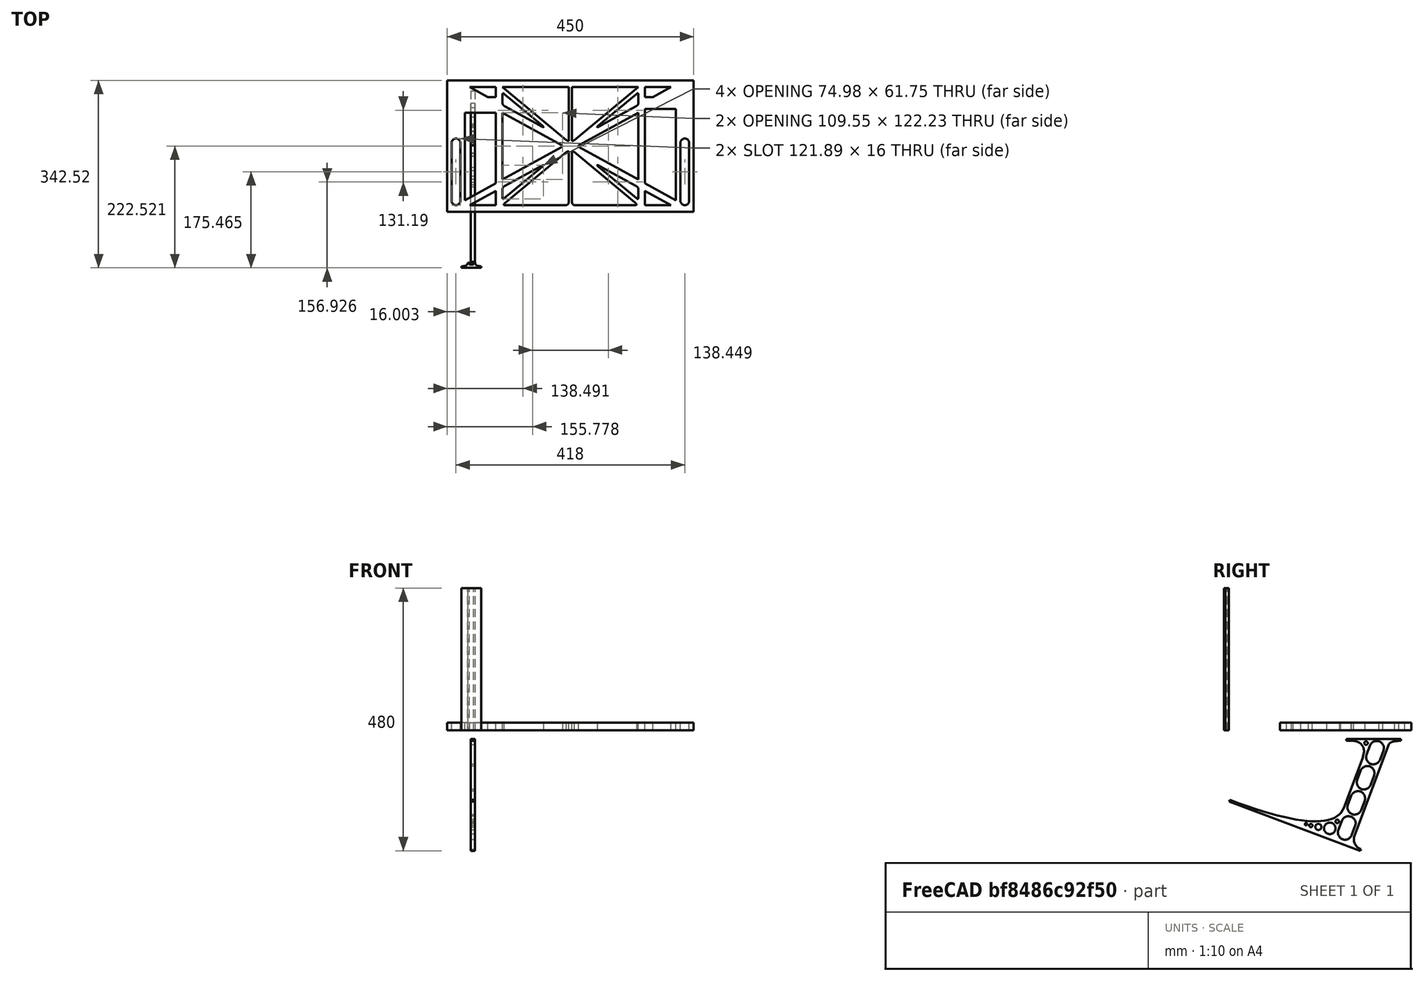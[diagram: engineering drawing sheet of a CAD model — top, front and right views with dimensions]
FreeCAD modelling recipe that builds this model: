
FCSTD DOCUMENT  (FreeCAD 0.19R0.19.2)
Label: laptopStand081
License: All rights reserved
LicenseURL: http://en.wikipedia.org/wiki/All_rights_reserved
objects: Sketcher::SketchObject×3, Part::Extrusion×3
note: 6 computed .brp shape members not serialized (recipe doc carries the construction recipe); baked Part::Feature solids carry a one-line shape summary decoded from their .brp

FEATURE [Sketcher::SketchObject] Sketch
  FullyConstrained = false
  sketch-geometry (204):
    g0: LineSegment StartX=-10.9272 StartY=-82.7794 StartZ=0 EndX=46.0728 EndY=-51.4823 EndZ=0
    g1: LineSegment StartX=366.073 StartY=-91.7794 StartZ=0 EndX=318.073 EndY=-65.424 EndZ=0
    g2: LineSegment StartX=-10.9272 StartY=77.3346 StartZ=0 EndX=-10.9272 EndY=-82.7794 EndZ=0
    g3: LineSegment StartX=375.073 StartY=-82.7794 StartZ=0 EndX=375.073 EndY=83.9235 EndZ=0
    g4: LineSegment StartX=-1.92719 StartY=-91.7794 StartZ=0 EndX=46.0728 EndY=-91.7794 EndZ=0
    g5: LineSegment StartX=318.073 StartY=124.221 StartZ=0 EndX=366.073 EndY=124.221 EndZ=0
    g6: LineSegment StartX=306.073 StartY=124.221 StartZ=0 EndX=189.124 EndY=27.0628 EndZ=0
    g7: LineSegment StartX=175.022 StartY=27.0628 StartZ=0 EndX=58.0728 EndY=124.221 EndZ=0
    g8: LineSegment StartX=306.073 StartY=77.3346 StartZ=0 EndX=306.073 EndY=-44.8935 EndZ=0
    g9: LineSegment StartX=318.073 StartY=83.9235 StartZ=0 EndX=318.073 EndY=-51.4823 EndZ=0
    g10: LineSegment StartX=318.073 StartY=-51.4823 StartZ=0 EndX=375.073 EndY=-82.7794 EndZ=0
    g11: LineSegment StartX=318.073 StartY=-65.424 StartZ=0 EndX=318.073 EndY=-91.7794 EndZ=0
    g12: LineSegment StartX=318.073 StartY=-91.7794 StartZ=0 EndX=366.073 EndY=-91.7794 EndZ=0
    g13: LineSegment StartX=58.0728 StartY=-44.8935 StartZ=0 EndX=58.0728 EndY=77.3346 EndZ=0
    g14: LineSegment StartX=46.0728 StartY=-65.424 StartZ=0 EndX=-1.92719 EndY=-91.7794 EndZ=0
    g15: LineSegment StartX=46.0728 StartY=-65.424 StartZ=0 EndX=46.0728 EndY=-91.7794 EndZ=0
    g16: LineSegment StartX=46.0728 StartY=77.3346 StartZ=0 EndX=46.0728 EndY=-51.4823 EndZ=0
    g17: LineSegment StartX=-42.9272 StartY=136.221 StartZ=0 EndX=-42.9272 EndY=-103.779 EndZ=0
    g18: LineSegment StartX=407.073 StartY=136.221 StartZ=0 EndX=407.073 EndY=-103.779 EndZ=0
    g19: LineSegment StartX=179.022 StartY=27.0628 StartZ=0 EndX=179.022 EndY=124.221 EndZ=0
    g20: LineSegment StartX=185.124 StartY=27.0628 StartZ=0 EndX=185.124 EndY=124.221 EndZ=0
    g21: ArcOfCircle CenterX=-26.9272 CenterY=22.1087 CenterZ=0 NormalX=0 NormalY=0 NormalZ=1 AngleXU=0 Radius=8 StartAngle=1e-16 EndAngle=3.14159
    g22: ArcOfCircle CenterX=-26.9272 CenterY=-83.7794 CenterZ=0 NormalX=0 NormalY=0 NormalZ=1 AngleXU=0 Radius=8 StartAngle=3.14159 EndAngle=6.28319
    g23: LineSegment StartX=-34.9272 StartY=22.1087 StartZ=0 EndX=-34.9272 EndY=-83.7794 EndZ=0
    g24: LineSegment StartX=-18.9272 StartY=22.1087 StartZ=0 EndX=-18.9272 EndY=-83.7794 EndZ=0
    g25: LineSegment StartX=306.073 StartY=124.221 StartZ=0 EndX=185.124 EndY=124.221 EndZ=0
    g26: LineSegment StartX=179.022 StartY=124.221 StartZ=0 EndX=58.0728 EndY=124.221 EndZ=0
    g27: ArcOfCircle CenterX=391.073 CenterY=22.1087 CenterZ=0 NormalX=0 NormalY=0 NormalZ=1 AngleXU=0 Radius=8 StartAngle=-4.4e-15 EndAngle=3.14159
    g28: LineSegment StartX=399.073 StartY=22.1087 StartZ=0 EndX=399.073 EndY=-83.7794 EndZ=0
    g29: LineSegment StartX=383.073 StartY=22.1087 StartZ=0 EndX=383.073 EndY=-83.7794 EndZ=0
    g30: ArcOfCircle CenterX=391.073 CenterY=-83.7794 CenterZ=0 NormalX=0 NormalY=0 NormalZ=1 AngleXU=0 Radius=8 StartAngle=3.14159 EndAngle=6.28319
    g31: Circle CenterX=175.022 CenterY=27.0628 CenterZ=0 NormalX=0 NormalY=0 NormalZ=1 AngleXU=0 Radius=1
    g32: Circle CenterX=179.022 CenterY=24.8665 CenterZ=0 NormalX=0 NormalY=0 NormalZ=1 AngleXU=0 Radius=1
    g33: Circle CenterX=179.022 CenterY=27.0628 CenterZ=0 NormalX=0 NormalY=0 NormalZ=1 AngleXU=0 Radius=1
    g34: BSplineCurve PolesCount=3 KnotsCount=2 Degree=2 IsPeriodic=0
    g35: GeomPoint X=175.022 Y=27.0628 Z=0
    g36: GeomPoint X=179.022 Y=27.0628 Z=0
    g37: Circle CenterX=189.124 CenterY=27.0628 CenterZ=0 NormalX=0 NormalY=0 NormalZ=1 AngleXU=0 Radius=1
    g38: Circle CenterX=185.124 CenterY=24.8665 CenterZ=0 NormalX=0 NormalY=0 NormalZ=1 AngleXU=0 Radius=1
    g39: Circle CenterX=185.124 CenterY=27.0628 CenterZ=0 NormalX=0 NormalY=0 NormalZ=1 AngleXU=0 Radius=1
    g40: BSplineCurve PolesCount=3 KnotsCount=2 Degree=2 IsPeriodic=0
    g41: GeomPoint X=189.124 Y=27.0628 Z=0
    g42: GeomPoint X=185.124 Y=27.0628 Z=0
    g43: Circle CenterX=175.022 CenterY=5.37834 CenterZ=0 NormalX=0 NormalY=0 NormalZ=1 AngleXU=0 Radius=1
    g44: Circle CenterX=179.022 CenterY=7.57463 CenterZ=0 NormalX=0 NormalY=0 NormalZ=1 AngleXU=0 Radius=1
    g45: Circle CenterX=179.022 CenterY=5.34704 CenterZ=0 NormalX=0 NormalY=0 NormalZ=1 AngleXU=0 Radius=1
    g46: BSplineCurve PolesCount=3 KnotsCount=2 Degree=2 IsPeriodic=0
    g47: GeomPoint X=175.022 Y=5.37834 Z=0
    g48: GeomPoint X=179.022 Y=5.34704 Z=0
    g49: Circle CenterX=189.124 CenterY=5.37834 CenterZ=0 NormalX=0 NormalY=0 NormalZ=1 AngleXU=0 Radius=1
    g50: Circle CenterX=185.124 CenterY=7.57463 CenterZ=0 NormalX=0 NormalY=0 NormalZ=1 AngleXU=0 Radius=1
    g51: Circle CenterX=185.124 CenterY=5.34704 CenterZ=0 NormalX=0 NormalY=0 NormalZ=1 AngleXU=0 Radius=1
    g52: BSplineCurve PolesCount=3 KnotsCount=2 Degree=2 IsPeriodic=0
    g53: GeomPoint X=189.124 Y=5.37834 Z=0
    g54: GeomPoint X=185.124 Y=5.34704 Z=0
    g55: Circle CenterX=165.871 CenterY=18.1458 CenterZ=0 NormalX=0 NormalY=0 NormalZ=1 AngleXU=0 Radius=1
    g56: Circle CenterX=169.377 CenterY=16.2206 CenterZ=0 NormalX=0 NormalY=0 NormalZ=1 AngleXU=0 Radius=1
    g57: Circle CenterX=165.871 CenterY=14.2954 CenterZ=0 NormalX=0 NormalY=0 NormalZ=1 AngleXU=0 Radius=1
    g58: BSplineCurve PolesCount=3 KnotsCount=2 Degree=2 IsPeriodic=0
    g59: GeomPoint X=165.871 Y=18.1458 Z=0
    g60: GeomPoint X=165.871 Y=14.2954 Z=0
    g61: Circle CenterX=198.275 CenterY=18.1458 CenterZ=0 NormalX=0 NormalY=0 NormalZ=1 AngleXU=0 Radius=1
    g62: Circle CenterX=194.768 CenterY=16.2206 CenterZ=0 NormalX=0 NormalY=0 NormalZ=1 AngleXU=0 Radius=1
    g63: Circle CenterX=198.275 CenterY=14.2954 CenterZ=0 NormalX=0 NormalY=0 NormalZ=1 AngleXU=0 Radius=1
    g64: BSplineCurve PolesCount=3 KnotsCount=2 Degree=2 IsPeriodic=0
    g65: GeomPoint X=198.275 Y=18.1458 Z=0
    g66: GeomPoint X=198.275 Y=14.2954 Z=0
    g67: LineSegment StartX=165.871 StartY=18.1458 StartZ=0 EndX=58.0728 EndY=77.3346 EndZ=0
    g68: LineSegment StartX=58.0728 StartY=-44.8935 StartZ=0 EndX=165.871 EndY=14.2954 EndZ=0
    g69: LineSegment StartX=198.275 StartY=18.1458 StartZ=0 EndX=306.073 EndY=77.3346 EndZ=0
    g70: LineSegment StartX=198.275 StartY=14.2954 StartZ=0 EndX=306.073 EndY=-44.8935 EndZ=0
    g71: LineSegment StartX=407.073 StartY=-103.779 StartZ=0 EndX=-42.9272 EndY=-103.779 EndZ=0
    g72: LineSegment StartX=407.073 StartY=136.221 StartZ=0 EndX=-42.9272 EndY=136.221 EndZ=0
    g73: LineSegment StartX=46.0728 StartY=77.3346 StartZ=0 EndX=-10.9272 EndY=77.3346 EndZ=0
    g74: LineSegment StartX=46.0728 StartY=105.865 StartZ=0 EndX=31.5028 EndY=105.865 EndZ=0
    g75: LineSegment StartX=46.0728 StartY=124.221 StartZ=0 EndX=46.0728 EndY=105.865 EndZ=0
    g76: LineSegment StartX=-1.92719 StartY=124.221 StartZ=0 EndX=31.5028 EndY=105.865 EndZ=0
    g77: LineSegment StartX=46.0728 StartY=124.221 StartZ=0 EndX=-1.92719 EndY=124.221 EndZ=0
    g78: LineSegment StartX=318.073 StartY=83.9235 StartZ=0 EndX=375.073 EndY=83.9235 EndZ=0
    g79: LineSegment StartX=318.073 StartY=105.865 StartZ=0 EndX=332.643 EndY=105.865 EndZ=0
    g80: LineSegment StartX=332.643 StartY=105.865 StartZ=0 EndX=366.073 EndY=124.221 EndZ=0
    g81: LineSegment StartX=318.073 StartY=124.221 StartZ=0 EndX=318.073 EndY=105.865 EndZ=0
    g82: Circle CenterX=125.607 CenterY=54.1951 CenterZ=0 NormalX=0 NormalY=0 NormalZ=1 AngleXU=0 Radius=1
    g83: Circle CenterX=139.632 CenterY=46.4944 CenterZ=0 NormalX=0 NormalY=0 NormalZ=1 AngleXU=0 Radius=1
    g84: Circle CenterX=127.326 CenterY=56.7187 CenterZ=0 NormalX=0 NormalY=0 NormalZ=1 AngleXU=0 Radius=1
    g85: BSplineCurve PolesCount=3 KnotsCount=2 Degree=2 IsPeriodic=0
    g86: GeomPoint X=125.607 Y=54.1951 Z=0
    g87: GeomPoint X=127.326 Y=56.7187 Z=0
    g88: Circle CenterX=236.821 CenterY=56.7187 CenterZ=0 NormalX=0 NormalY=0 NormalZ=1 AngleXU=0 Radius=1
    g89: Circle CenterX=224.513 CenterY=46.4944 CenterZ=0 NormalX=0 NormalY=0 NormalZ=1 AngleXU=0 Radius=1
    g90: Circle CenterX=238.538 CenterY=54.1951 CenterZ=0 NormalX=0 NormalY=0 NormalZ=1 AngleXU=0 Radius=1
    g91: BSplineCurve PolesCount=3 KnotsCount=2 Degree=2 IsPeriodic=0
    g92: GeomPoint X=236.821 Y=56.7187 Z=0
    g93: GeomPoint X=238.538 Y=54.1951 Z=0
    g94: Circle CenterX=238.538 CenterY=-21.7539 CenterZ=0 NormalX=0 NormalY=0 NormalZ=1 AngleXU=0 Radius=1
    g95: Circle CenterX=224.513 CenterY=-14.0532 CenterZ=0 NormalX=0 NormalY=0 NormalZ=1 AngleXU=0 Radius=1
    g96: Circle CenterX=236.821 CenterY=-24.2775 CenterZ=0 NormalX=0 NormalY=0 NormalZ=1 AngleXU=0 Radius=1
    g97: BSplineCurve PolesCount=3 KnotsCount=2 Degree=2 IsPeriodic=0
    g98: GeomPoint X=238.538 Y=-21.7539 Z=0
    g99: GeomPoint X=236.821 Y=-24.2775 Z=0
    g100: Circle CenterX=125.607 CenterY=-21.7539 CenterZ=0 NormalX=0 NormalY=0 NormalZ=1 AngleXU=0 Radius=1
    g101: Circle CenterX=139.632 CenterY=-14.0532 CenterZ=0 NormalX=0 NormalY=0 NormalZ=1 AngleXU=0 Radius=1
    g102: Circle CenterX=127.325 CenterY=-24.2775 CenterZ=0 NormalX=0 NormalY=0 NormalZ=1 AngleXU=0 Radius=1
    g103: BSplineCurve PolesCount=3 KnotsCount=2 Degree=2 IsPeriodic=0
    g104: GeomPoint X=125.607 Y=-21.7539 Z=0
    g105: GeomPoint X=127.325 Y=-24.2775 Z=0
    g106: Circle CenterX=302.996 CenterY=111.695 CenterZ=0 NormalX=0 NormalY=0 NormalZ=1 AngleXU=0 Radius=1
    g107: Circle CenterX=306.073 CenterY=114.251 CenterZ=0 NormalX=0 NormalY=0 NormalZ=1 AngleXU=0 Radius=1
    g108: Circle CenterX=306.073 CenterY=110.251 CenterZ=0 NormalX=0 NormalY=0 NormalZ=1 AngleXU=0 Radius=1
    g109: BSplineCurve PolesCount=3 KnotsCount=2 Degree=2 IsPeriodic=0
    g110: GeomPoint X=302.996 Y=111.695 Z=0
    g111: GeomPoint X=306.073 Y=110.251 Z=0
    g112: Circle CenterX=306.073 CenterY=95.2763 CenterZ=0 NormalX=0 NormalY=0 NormalZ=1 AngleXU=0 Radius=1
    g113: Circle CenterX=306.073 CenterY=91.2763 CenterZ=0 NormalX=0 NormalY=0 NormalZ=1 AngleXU=0 Radius=1
    g114: Circle CenterX=302.567 CenterY=89.3511 CenterZ=0 NormalX=0 NormalY=0 NormalZ=1 AngleXU=0 Radius=1
    g115: BSplineCurve PolesCount=3 KnotsCount=2 Degree=2 IsPeriodic=0
    g116: GeomPoint X=306.073 Y=95.2763 Z=0
    g117: GeomPoint X=302.567 Y=89.3511 Z=0
    g118: LineSegment StartX=306.073 StartY=110.251 StartZ=0 EndX=306.073 EndY=95.2763 EndZ=0
    g119: LineSegment StartX=302.996 StartY=111.695 StartZ=0 EndX=236.821 EndY=56.7187 EndZ=0
    g120: LineSegment StartX=238.538 StartY=54.1951 StartZ=0 EndX=302.567 EndY=89.3511 EndZ=0
    g121: Circle CenterX=61.1496 CenterY=111.695 CenterZ=0 NormalX=0 NormalY=0 NormalZ=1 AngleXU=0 Radius=1
    g122: Circle CenterX=58.0728 CenterY=114.251 CenterZ=0 NormalX=0 NormalY=0 NormalZ=1 AngleXU=0 Radius=1
    g123: Circle CenterX=58.0728 CenterY=110.251 CenterZ=0 NormalX=0 NormalY=0 NormalZ=1 AngleXU=0 Radius=1
    g124: BSplineCurve PolesCount=3 KnotsCount=2 Degree=2 IsPeriodic=0
    g125: GeomPoint X=61.1496 Y=111.695 Z=0
    g126: GeomPoint X=58.0728 Y=110.251 Z=0
    g127: Circle CenterX=61.5791 CenterY=89.3511 CenterZ=0 NormalX=0 NormalY=0 NormalZ=1 AngleXU=0 Radius=1
    g128: Circle CenterX=58.0728 CenterY=91.2763 CenterZ=0 NormalX=0 NormalY=0 NormalZ=1 AngleXU=0 Radius=1
    g129: Circle CenterX=58.0728 CenterY=95.2763 CenterZ=0 NormalX=0 NormalY=0 NormalZ=1 AngleXU=0 Radius=1
    g130: BSplineCurve PolesCount=3 KnotsCount=2 Degree=2 IsPeriodic=0
    g131: GeomPoint X=61.5791 Y=89.3511 Z=0
    g132: GeomPoint X=58.0728 Y=95.2763 Z=0
    g133: LineSegment StartX=58.0728 StartY=110.251 StartZ=0 EndX=58.0728 EndY=95.2763 EndZ=0
    g134: LineSegment StartX=61.1496 StartY=111.695 StartZ=0 EndX=127.326 EndY=56.7187 EndZ=0
    g135: LineSegment StartX=125.607 StartY=54.1951 StartZ=0 EndX=61.5791 EndY=89.3511 EndZ=0
    g136: Circle CenterX=61.5791 CenterY=-56.9099 CenterZ=0 NormalX=0 NormalY=0 NormalZ=1 AngleXU=0 Radius=1
    g137: Circle CenterX=58.0728 CenterY=-58.8351 CenterZ=0 NormalX=0 NormalY=0 NormalZ=1 AngleXU=0 Radius=1
    g138: Circle CenterX=58.0728 CenterY=-62.8351 CenterZ=0 NormalX=0 NormalY=0 NormalZ=1 AngleXU=0 Radius=1
    g139: BSplineCurve PolesCount=3 KnotsCount=2 Degree=2 IsPeriodic=0
    g140: GeomPoint X=61.5791 Y=-56.9099 Z=0
    g141: GeomPoint X=58.0728 Y=-62.8351 Z=0
    g142: Circle CenterX=58.0728 CenterY=-77.8102 CenterZ=0 NormalX=0 NormalY=0 NormalZ=1 AngleXU=0 Radius=1
    g143: Circle CenterX=58.0728 CenterY=-81.8102 CenterZ=0 NormalX=0 NormalY=0 NormalZ=1 AngleXU=0 Radius=1
    g144: Circle CenterX=61.1496 CenterY=-79.2541 CenterZ=0 NormalX=0 NormalY=0 NormalZ=1 AngleXU=0 Radius=1
    g145: BSplineCurve PolesCount=3 KnotsCount=2 Degree=2 IsPeriodic=0
    g146: GeomPoint X=58.0728 Y=-77.8102 Z=0
    g147: GeomPoint X=61.1496 Y=-79.2541 Z=0
    g148: LineSegment StartX=58.0728 StartY=-62.8351 StartZ=0 EndX=58.0728 EndY=-77.8102 EndZ=0
    g149: LineSegment StartX=61.1496 StartY=-79.2541 StartZ=0 EndX=127.325 EndY=-24.2775 EndZ=0
    g150: LineSegment StartX=125.607 StartY=-21.7539 StartZ=0 EndX=61.5791 EndY=-56.9099 EndZ=0
    g151: Circle CenterX=302.567 CenterY=-56.9099 CenterZ=0 NormalX=0 NormalY=0 NormalZ=1 AngleXU=0 Radius=1
    g152: Circle CenterX=306.073 CenterY=-58.8351 CenterZ=0 NormalX=0 NormalY=0 NormalZ=1 AngleXU=0 Radius=1
    g153: Circle CenterX=306.073 CenterY=-62.8351 CenterZ=0 NormalX=0 NormalY=0 NormalZ=1 AngleXU=0 Radius=1
    g154: BSplineCurve PolesCount=3 KnotsCount=2 Degree=2 IsPeriodic=0
    g155: GeomPoint X=302.567 Y=-56.9099 Z=0
    g156: GeomPoint X=306.073 Y=-62.8351 Z=0
    g157: Circle CenterX=302.996 CenterY=-79.2541 CenterZ=0 NormalX=0 NormalY=0 NormalZ=1 AngleXU=0 Radius=1
    g158: Circle CenterX=306.073 CenterY=-81.8102 CenterZ=0 NormalX=0 NormalY=0 NormalZ=1 AngleXU=0 Radius=1
    g159: Circle CenterX=306.073 CenterY=-77.8102 CenterZ=0 NormalX=0 NormalY=0 NormalZ=1 AngleXU=0 Radius=1
    g160: BSplineCurve PolesCount=3 KnotsCount=2 Degree=2 IsPeriodic=0
    g161: GeomPoint X=302.996 Y=-79.2541 Z=0
    g162: GeomPoint X=306.073 Y=-77.8102 Z=0
    g163: LineSegment StartX=306.073 StartY=-62.8351 StartZ=0 EndX=306.073 EndY=-77.8102 EndZ=0
    g164: LineSegment StartX=302.996 StartY=-79.2541 StartZ=0 EndX=236.821 EndY=-24.2775 EndZ=0
    g165: LineSegment StartX=238.538 StartY=-21.7539 StartZ=0 EndX=302.567 EndY=-56.9099 EndZ=0
    g166: Circle CenterX=61.6457 CenterY=-88.8112 CenterZ=0 NormalX=0 NormalY=0 NormalZ=1 AngleXU=0 Radius=1
    g167: Circle CenterX=58.0728 CenterY=-91.7794 CenterZ=0 NormalX=0 NormalY=0 NormalZ=1 AngleXU=0 Radius=1
    g168: Circle CenterX=63.9135 CenterY=-91.7794 CenterZ=0 NormalX=0 NormalY=0 NormalZ=1 AngleXU=0 Radius=1
    g169: BSplineCurve PolesCount=3 KnotsCount=2 Degree=2 IsPeriodic=0
    g170: GeomPoint X=61.6457 Y=-88.8112 Z=0
    g171: GeomPoint X=63.9135 Y=-91.7794 Z=0
    g172: Circle CenterX=179.022 CenterY=-85.8163 CenterZ=0 NormalX=0 NormalY=0 NormalZ=1 AngleXU=0 Radius=1
    g173: Circle CenterX=179.022 CenterY=-91.7794 CenterZ=0 NormalX=0 NormalY=0 NormalZ=1 AngleXU=0 Radius=1
    g174: Circle CenterX=171.895 CenterY=-91.7794 CenterZ=0 NormalX=0 NormalY=0 NormalZ=1 AngleXU=0 Radius=1
    g175: BSplineCurve PolesCount=3 KnotsCount=2 Degree=2 IsPeriodic=0
    g176: GeomPoint X=179.022 Y=-85.8163 Z=0
    g177: GeomPoint X=171.895 Y=-91.7794 Z=0
    g178: Circle CenterX=185.124 CenterY=-86.2028 CenterZ=0 NormalX=0 NormalY=0 NormalZ=1 AngleXU=0 Radius=1
    g179: Circle CenterX=185.124 CenterY=-91.7794 CenterZ=0 NormalX=0 NormalY=0 NormalZ=1 AngleXU=0 Radius=1
    g180: Circle CenterX=191.747 CenterY=-91.7794 CenterZ=0 NormalX=0 NormalY=0 NormalZ=1 AngleXU=0 Radius=1
    g181: BSplineCurve PolesCount=3 KnotsCount=2 Degree=2 IsPeriodic=0
    g182: GeomPoint X=185.124 Y=-86.2028 Z=0
    g183: GeomPoint X=191.747 Y=-91.7794 Z=0
    g184: Circle CenterX=299.888 CenterY=-86.6413 CenterZ=0 NormalX=0 NormalY=0 NormalZ=1 AngleXU=0 Radius=1
    g185: Circle CenterX=306.073 CenterY=-91.7794 CenterZ=0 NormalX=0 NormalY=0 NormalZ=1 AngleXU=0 Radius=1
    g186: Circle CenterX=298.776 CenterY=-91.7794 CenterZ=0 NormalX=0 NormalY=0 NormalZ=1 AngleXU=0 Radius=1
    g187: BSplineCurve PolesCount=3 KnotsCount=2 Degree=2 IsPeriodic=0
    g188: GeomPoint X=299.888 Y=-86.6413 Z=0
    g189: GeomPoint X=298.776 Y=-91.7794 Z=0
    g190: LineSegment StartX=189.124 StartY=5.37834 StartZ=0 EndX=299.888 EndY=-86.6413 EndZ=0
    g191: LineSegment StartX=298.776 StartY=-91.7794 StartZ=0 EndX=191.747 EndY=-91.7794 EndZ=0
    g192: LineSegment StartX=185.124 StartY=-86.2028 StartZ=0 EndX=185.124 EndY=5.34704 EndZ=0
    g193: LineSegment StartX=179.022 StartY=5.34704 StartZ=0 EndX=179.022 EndY=-85.8163 EndZ=0
    g194: LineSegment StartX=171.895 StartY=-91.7794 StartZ=0 EndX=63.9135 EndY=-91.7794 EndZ=0
    g195: LineSegment StartX=61.6457 StartY=-88.8112 StartZ=0 EndX=175.022 EndY=5.37834 EndZ=0
    g196: LineSegment StartX=306.48 StartY=122.126 StartZ=0 EndX=303.085 EndY=119.306 EndZ=0
    g197: LineSegment StartX=305.705 StartY=125.431 StartZ=0 EndX=296.607 EndY=125.431 EndZ=0
    g198: LineSegment StartX=185.963 StartY=125.477 StartZ=0 EndX=193.087 EndY=125.477 EndZ=0
    g199: LineSegment StartX=184.375 StartY=122.473 StartZ=0 EndX=184.375 EndY=115.263 EndZ=0
    g200: LineSegment StartX=179.954 StartY=122.387 StartZ=0 EndX=179.954 EndY=116.379 EndZ=0
    g201: LineSegment StartX=178.581 StartY=125.133 StartZ=0 EndX=173.045 EndY=125.133 EndZ=0
    g202: LineSegment StartX=59.3542 StartY=125.179 StartZ=0 EndX=65.4913 EndY=125.179 EndZ=0
    g203: LineSegment StartX=59.239 StartY=121.678 StartZ=0 EndX=63.847 EndY=117.85 EndZ=0
  constraints (347):
    c: Horizontal(g4)
    c: Horizontal(g5)
    c: Coincident(g9,g10)
    c: Coincident(g11,g1)
    c: Tangent(g9,g11)
    c: Coincident(g15,g14)
    c: Coincident(g0,g16)
    c: Block(g7)
    c: Block(g6)
    c: Block(g10)
    c: Block(g3)
    c: Block(g1)
    c: Block(g11)
    c: Block(g15)
    c: Block(g14)
    c: Block(g0)
    c: Block(g2)
    c: Block(g8)
    c: Block(g5)
    c: Block(g12)
    c: Block(g4)
    c: Vertical(g17)
    c: Vertical(g18)
    c: Block(g18)
    c: Block(g17)
    c: Vertical(g19)
    c: Vertical(g20)
    c: Block(g19)
    c: Block(g20)
    c: Tangent(g21,g24) = 1.5708
    c: Tangent(g21,g23) = -1.5708
    c: Tangent(g23,g22) = -1.5708
    c: Tangent(g24,g22) = 1.5708
    c: Vertical(g23)
    c: Equal(g21,g22)
    c: Block(g24)
    c: Block(g23)
    c: Coincident(g25,g6)
    c: Coincident(g25,g20)
    c: Horizontal(g25)
    c: Coincident(g26,g19)
    c: Coincident(g26,g7)
    c: Horizontal(g26)
    c: Tangent(g27,g28) = 1.5708
    c: Tangent(g28,g30) = 1.5708
    c: Equal(g27,g30)
    c: Coincident(g29,g27)
    c: Coincident(g29,g30)
    c: Block(g28)
    c: Block(g29)
    c: Coincident(g34,g7)
    c: Weight(g31) = 1
    c: Equal(g31,g32)
    c: Equal(g31,g33)
    c: Coincident(g34,g19)
    c: InternalAlignment(g31,g34)
    c: InternalAlignment(g32,g34)
    c: InternalAlignment(g33,g34)
    c: InternalAlignment(g35,g34)
    c: InternalAlignment(g36,g34)
    c: Coincident(g40,g6)
    c: Weight(g37) = 1
    c: Equal(g37,g38)
    c: Equal(g37,g39)
    c: Coincident(g40,g20)
    c: InternalAlignment(g37,g40)
    c: InternalAlignment(g38,g40)
    c: InternalAlignment(g39,g40)
    c: InternalAlignment(g41,g40)
    c: InternalAlignment(g42,g40)
    c: Block(g40)
    c: Block(g34)
    c: Weight(g43) = 1
    c: Equal(g43,g44)
    c: Equal(g43,g45)
    c: InternalAlignment(g43,g46)
    c: InternalAlignment(g44,g46)
    c: InternalAlignment(g45,g46)
    c: InternalAlignment(g47,g46)
    c: InternalAlignment(g48,g46)
    c: Weight(g49) = 1
    c: Equal(g49,g50)
    c: Equal(g49,g51)
    c: InternalAlignment(g49,g52)
    c: InternalAlignment(g50,g52)
    c: InternalAlignment(g51,g52)
    c: InternalAlignment(g53,g52)
    c: InternalAlignment(g54,g52)
    c: Block(g52)
    c: Block(g46)
    c: Weight(g55) = 1
    c: Equal(g55,g56)
    c: Equal(g55,g57)
    c: InternalAlignment(g55,g58)
    c: InternalAlignment(g56,g58)
    c: InternalAlignment(g57,g58)
    c: InternalAlignment(g59,g58)
    c: InternalAlignment(g60,g58)
    c: Weight(g61) = 1
    c: Equal(g61,g62)
    c: Equal(g61,g63)
    c: InternalAlignment(g61,g64)
    c: InternalAlignment(g62,g64)
    c: InternalAlignment(g63,g64)
    c: InternalAlignment(g65,g64)
    c: InternalAlignment(g66,g64)
    c: Block(g58)
    c: Block(g64)
    c: Coincident(g67,g58)
    c: Coincident(g67,g13)
    c: Coincident(g68,g13)
    c: Coincident(g68,g58)
    c: Coincident(g69,g64)
    c: Coincident(g69,g8)
    c: Coincident(g70,g64)
    c: Coincident(g70,g8)
    c: Block(g13)
    c: Coincident(g71,g18)
    c: Coincident(g71,g17)
    c: Horizontal(g71)
    c: Distance(g71) = 450
    c: Coincident(g72,g18)
    c: Coincident(g72,g17)
    c: Horizontal(g72)
    c: Horizontal(g73)
    c: Coincident(g16,g73)
    c: Horizontal(g74)
    c: Vertical(g75)
    c: Block(g75)
    c: Block(g74)
    c: Block(g73)
    c: Distance(g75) = 18.3554
    c: Coincident(g77,g75)
    c: Coincident(g77,g76)
    c: Horizontal(g77)
    c: Block(g77)
    c: Block(g76)
    c: Coincident(g74,g76)
    c: Coincident(g2,g73)
    c: Coincident(g78,g9)
    c: Horizontal(g78)
    c: Horizontal(g79)
    c: Block(g78)
    c: Coincident(g80,g5)
    c: Coincident(g81,g5)
    c: Coincident(g81,g79)
    c: Vertical(g81)
    c: Block(g81)
    c: Coincident(g79,g80)
    c: Block(g80)
    c: Coincident(g3,g78)
    c: Weight(g82) = 1
    c: Equal(g82,g83)
    c: Equal(g82,g84)
    c: InternalAlignment(g82,g85)
    c: InternalAlignment(g83,g85)
    c: InternalAlignment(g84,g85)
    c: InternalAlignment(g86,g85)
    c: InternalAlignment(g87,g85)
    c: Block(g85)
    c: Weight(g88) = 1
    c: Equal(g88,g89)
    c: Equal(g88,g90)
    c: InternalAlignment(g88,g91)
    c: InternalAlignment(g89,g91)
    c: InternalAlignment(g90,g91)
    c: InternalAlignment(g92,g91)
    c: InternalAlignment(g93,g91)
    c: Block(g91)
    c: Weight(g94) = 1
    c: Equal(g94,g95)
    c: Equal(g94,g96)
    c: InternalAlignment(g94,g97)
    c: InternalAlignment(g95,g97)
    c: InternalAlignment(g96,g97)
    c: InternalAlignment(g98,g97)
    c: InternalAlignment(g99,g97)
    c: Block(g97)
    c: Weight(g100) = 1
    c: Equal(g100,g101)
    c: Equal(g100,g102)
    c: InternalAlignment(g100,g103)
    c: InternalAlignment(g101,g103)
    c: InternalAlignment(g102,g103)
    c: InternalAlignment(g104,g103)
    c: InternalAlignment(g105,g103)
    c: Block(g103)
    c: Weight(g106) = 1
    c: Equal(g106,g107)
    c: Equal(g106,g108)
    c: InternalAlignment(g106,g109)
    c: InternalAlignment(g107,g109)
    c: InternalAlignment(g108,g109)
    c: InternalAlignment(g110,g109)
    c: InternalAlignment(g111,g109)
    c: Weight(g112) = 1
    c: Equal(g112,g113)
    c: Equal(g112,g114)
    c: InternalAlignment(g112,g115)
    c: InternalAlignment(g113,g115)
    c: InternalAlignment(g114,g115)
    c: InternalAlignment(g116,g115)
    c: InternalAlignment(g117,g115)
    c: Block(g109)
    c: Block(g115)
    c: Coincident(g118,g109)
    c: Coincident(g118,g115)
    c: Vertical(g118)
    c: Coincident(g119,g109)
    c: Coincident(g119,g91)
    c: Coincident(g120,g91)
    c: Coincident(g120,g115)
    c: Weight(g121) = 1
    c: Equal(g121,g122)
    c: Equal(g121,g123)
    c: InternalAlignment(g121,g124)
    c: InternalAlignment(g122,g124)
    c: InternalAlignment(g123,g124)
    c: InternalAlignment(g125,g124)
    c: InternalAlignment(g126,g124)
    c: Weight(g127) = 1
    c: Equal(g127,g128)
    c: Equal(g127,g129)
    c: InternalAlignment(g127,g130)
    c: InternalAlignment(g128,g130)
    c: InternalAlignment(g129,g130)
    c: InternalAlignment(g131,g130)
    c: InternalAlignment(g132,g130)
    c: Block(g124)
    c: Block(g130)
    c: Coincident(g133,g124)
    c: Coincident(g133,g130)
    c: Vertical(g133)
    c: Coincident(g134,g124)
    c: Coincident(g134,g85)
    c: Coincident(g135,g85)
    c: Coincident(g135,g130)
    c: Weight(g136) = 1
    c: Equal(g136,g137)
    c: Equal(g136,g138)
    c: InternalAlignment(g136,g139)
    c: InternalAlignment(g137,g139)
    c: InternalAlignment(g138,g139)
    c: InternalAlignment(g140,g139)
    c: InternalAlignment(g141,g139)
    c: Weight(g142) = 1
    c: Equal(g142,g143)
    c: Equal(g142,g144)
    c: InternalAlignment(g142,g145)
    c: InternalAlignment(g143,g145)
    c: InternalAlignment(g144,g145)
    c: InternalAlignment(g146,g145)
    c: InternalAlignment(g147,g145)
    c: Block(g139)
    c: Block(g145)
    c: Coincident(g148,g139)
    c: Coincident(g148,g145)
    c: Vertical(g148)
    c: Coincident(g149,g145)
    c: Coincident(g149,g103)
    c: Coincident(g150,g103)
    c: Coincident(g150,g139)
    c: Weight(g151) = 1
    c: Equal(g151,g152)
    c: Equal(g151,g153)
    c: InternalAlignment(g151,g154)
    c: InternalAlignment(g152,g154)
    c: InternalAlignment(g153,g154)
    c: InternalAlignment(g155,g154)
    c: InternalAlignment(g156,g154)
    c: Weight(g157) = 1
    c: Equal(g157,g158)
    c: Equal(g157,g159)
    c: InternalAlignment(g157,g160)
    c: InternalAlignment(g158,g160)
    c: InternalAlignment(g159,g160)
    c: InternalAlignment(g161,g160)
    c: InternalAlignment(g162,g160)
    c: Block(g154)
    c: Block(g160)
    c: Coincident(g163,g154)
    c: Coincident(g163,g160)
    c: Vertical(g163)
    c: Coincident(g164,g160)
    c: Coincident(g164,g97)
    c: Coincident(g165,g97)
    c: Coincident(g165,g154)
    c: Weight(g166) = 1
    c: Equal(g166,g167)
    c: Equal(g166,g168)
    c: InternalAlignment(g166,g169)
    c: InternalAlignment(g167,g169)
    c: InternalAlignment(g168,g169)
    c: InternalAlignment(g170,g169)
    c: InternalAlignment(g171,g169)
    c: Weight(g172) = 1
    c: Equal(g172,g173)
    c: Equal(g172,g174)
    c: InternalAlignment(g172,g175)
    c: InternalAlignment(g173,g175)
    c: InternalAlignment(g174,g175)
    c: InternalAlignment(g176,g175)
    c: InternalAlignment(g177,g175)
    c: Weight(g178) = 1
    c: Equal(g178,g179)
    c: Equal(g178,g180)
    c: InternalAlignment(g178,g181)
    c: InternalAlignment(g179,g181)
    c: InternalAlignment(g180,g181)
    c: InternalAlignment(g182,g181)
    c: InternalAlignment(g183,g181)
    c: Weight(g184) = 1
    c: Equal(g184,g185)
    c: Equal(g184,g186)
    c: InternalAlignment(g184,g187)
    c: InternalAlignment(g185,g187)
    c: InternalAlignment(g186,g187)
    c: InternalAlignment(g188,g187)
    c: InternalAlignment(g189,g187)
    c: Block(g187)
    c: Block(g181)
    c: Block(g175)
    c: Block(g169)
    c: Coincident(g190,g52)
    c: Coincident(g190,g187)
    c: Coincident(g191,g187)
    c: Coincident(g191,g181)
    c: Horizontal(g191)
    c: Coincident(g192,g181)
    c: Coincident(g192,g52)
    c: Vertical(g192)
    c: Coincident(g193,g46)
    c: Coincident(g193,g175)
    c: Vertical(g193)
    c: Coincident(g194,g175)
    c: Coincident(g194,g169)
    c: Horizontal(g194)
    c: Coincident(g195,g169)
    c: Coincident(g195,g46)
    c: Horizontal(g197)
    c: Horizontal(g198)
    c: Vertical(g199)
    c: Vertical(g200)
    c: Horizontal(g201)
    c: Horizontal(g202)
    c: Parallel(g203,g7)
    c: Parallel(g196,g6)
FEATURE [Sketcher::SketchObject] Sketch001
  FullyConstrained = true
  MapMode = 4
  Placement = pos=(0,0,0) rot=(0.57735,0.57735,0.57735;2.0944rad)
  Support = -> [Sketch]
  sketch-geometry (46):
    g0: BSplineCurve PolesCount=3 KnotsCount=2 Degree=2 IsPeriodic=0
    g1: ArcOfCircle CenterX=73.1223 CenterY=-32.291 CenterZ=0 NormalX=0 NormalY=0 NormalZ=1 AngleXU=0 Radius=13 StartAngle=5.92268 EndAngle=9.06428
    g2: ArcOfCircle CenterX=66.7816 CenterY=-49.1439 CenterZ=0 NormalX=0 NormalY=0 NormalZ=1 AngleXU=0 Radius=13 StartAngle=2.78068 EndAngle=5.92131
    g3: ArcOfCircle CenterX=55.9263 CenterY=-78.1807 CenterZ=0 NormalX=0 NormalY=0 NormalZ=1 AngleXU=0 Radius=13 StartAngle=5.92268 EndAngle=9.06428
    g4: ArcOfCircle CenterX=49.5884 CenterY=-95.0342 CenterZ=0 NormalX=0 NormalY=0 NormalZ=1 AngleXU=0 Radius=13 StartAngle=2.78068 EndAngle=5.92131
    g5: ArcOfCircle CenterX=38.7206 CenterY=-124.067 CenterZ=0 NormalX=0 NormalY=0 NormalZ=1 AngleXU=0 Radius=13 StartAngle=5.92268 EndAngle=9.06428
    g6: ArcOfCircle CenterX=32.3875 CenterY=-140.92 CenterZ=0 NormalX=0 NormalY=0 NormalZ=1 AngleXU=0 Radius=13 StartAngle=2.78068 EndAngle=5.92131
    g7: ArcOfCircle CenterX=21.4715 CenterY=-169.934 CenterZ=0 NormalX=0 NormalY=0 NormalZ=1 AngleXU=0 Radius=13 StartAngle=5.92268 EndAngle=9.06428
    g8: ArcOfCircle CenterX=15.1336 CenterY=-186.787 CenterZ=0 NormalX=0 NormalY=0 NormalZ=1 AngleXU=0 Radius=13 StartAngle=2.78068 EndAngle=5.92131
    g9-g12: Circle x4 (B-spline internal-alignment scaffolding for g13; pole/knot coordinates omitted)
    g13: BSplineCurve PolesCount=4 KnotsCount=2 Degree=3 IsPeriodic=0
    g14: GeomPoint X=28.8094 Y=-19.0875 Z=0
    g15: GeomPoint X=47.0443 Y=-50.4712 Z=0
    g16: Circle CenterX=53.5586 CenterY=-23.2695 CenterZ=0 NormalX=0 NormalY=0 NormalZ=1 AngleXU=0 Radius=3.24518
    g17: Circle CenterX=-195.441 CenterY=-127.082 CenterZ=0 NormalX=0 NormalY=0 NormalZ=1 AngleXU=0 Radius=1
    g18: Circle CenterX=-8.24091 CenterY=-197.481 CenterZ=0 NormalX=0 NormalY=0 NormalZ=1 AngleXU=0 Radius=1
    g19: Circle CenterX=12.8789 CenterY=-141.321 CenterZ=0 NormalX=0 NormalY=0 NormalZ=1 AngleXU=0 Radius=1
    g20: BSplineCurve PolesCount=3 KnotsCount=2 Degree=2 IsPeriodic=0
    g21: GeomPoint X=-195.441 Y=-127.082 Z=0
    g22: GeomPoint X=12.8789 Y=-141.321 Z=0
    g23: Circle CenterX=-12.8016 CenterY=-179.036 CenterZ=0 NormalX=0 NormalY=0 NormalZ=1 AngleXU=0 Radius=10.5072
    g24: Circle CenterX=0.933922 CenterY=-166.43 CenterZ=0 NormalX=0 NormalY=0 NormalZ=1 AngleXU=0 Radius=3.26661
    g25: Circle CenterX=-33.5518 CenterY=-176.44 CenterZ=0 NormalX=0 NormalY=0 NormalZ=1 AngleXU=0 Radius=5.64388
    g26: Circle CenterX=-47.2366 CenterY=-173.859 CenterZ=0 NormalX=0 NormalY=0 NormalZ=1 AngleXU=0 Radius=3.01653
    g27: Circle CenterX=-56.2595 CenterY=-171.456 CenterZ=0 NormalX=0 NormalY=0 NormalZ=1 AngleXU=0 Radius=2.12826
    g28: ArcOfCircle CenterX=51.2151 CenterY=-198.473 CenterZ=0 NormalX=0 NormalY=0 NormalZ=1 AngleXU=0 Radius=20 StartAngle=2.78189 EndAngle=4.35269
    g29: LineSegment StartX=32.4951 StartY=-191.433 StartZ=0 EndX=94.6578 EndY=-26.1352 EndZ=0
    g30: LineSegment StartX=43.1192 StartY=-220.001 StartZ=0 EndX=-196.497 EndY=-129.89 EndZ=0
    g31: LineSegment StartX=43.1192 StartY=-220.001 StartZ=0 EndX=44.1752 EndY=-217.193 EndZ=0
    g32: LineSegment StartX=117.223 StartY=-19.0875 StartZ=0 EndX=117.223 EndY=-16.0875 EndZ=0
    g33: LineSegment StartX=117.223 StartY=-16.0875 StartZ=0 EndX=17.2232 EndY=-16.0875 EndZ=0
    g34: LineSegment StartX=17.2232 StartY=-16.0875 StartZ=0 EndX=17.2232 EndY=-19.0875 EndZ=0
    g35: LineSegment StartX=28.8094 StartY=-19.0875 StartZ=0 EndX=17.2232 EndY=-19.0875 EndZ=0
    g36: LineSegment StartX=47.0443 StartY=-50.4712 StartZ=0 EndX=12.8789 EndY=-141.321 EndZ=0
    g37: LineSegment StartX=-195.441 StartY=-127.082 StartZ=0 EndX=-196.497 EndY=-129.89 EndZ=0
    g38: LineSegment StartX=85.2866 StartY=-36.8766 StartZ=0 EndX=78.9396 EndY=-53.7463 EndZ=0
    g39: LineSegment StartX=60.9579 StartY=-27.7053 StartZ=0 EndX=54.6191 EndY=-44.5532 EndZ=0
    g40: LineSegment StartX=68.0907 StartY=-82.7664 StartZ=0 EndX=61.7465 EndY=-99.6365 EndZ=0
    g41: LineSegment StartX=43.7619 StartY=-73.595 StartZ=0 EndX=37.426 EndY=-90.4435 EndZ=0
    g42: LineSegment StartX=50.885 StartY=-128.652 StartZ=0 EndX=44.5456 EndY=-145.522 EndZ=0
    g43: LineSegment StartX=26.5562 StartY=-119.481 StartZ=0 EndX=20.2251 EndY=-136.329 EndZ=0
    g44: LineSegment StartX=9.3071 StartY=-165.349 StartZ=0 EndX=2.97115 EndY=-182.197 EndZ=0
    g45: LineSegment StartX=33.6358 StartY=-174.52 StartZ=0 EndX=27.2917 EndY=-191.39 EndZ=0
  constraints (71):
    c: Block(g0)
    c: Block(g1)
    c: Block(g2)
    c: Block(g4)
    c: Block(g3)
    c: Block(g6)
    c: Block(g5)
    c: Block(g8)
    c: Block(g7)
    c: Weight(g9) = 1
    c: Equal(g9,g10)
    c: Equal(g9,g11)
    c: Equal(g9,g12)
    c: InternalAlignment(g9-g12 -> g13) x4
    c: InternalAlignment(g14,g13)
    c: InternalAlignment(g15,g13)
    c: Block(g16)
    c: Weight(g17) = 1
    c: Equal(g17,g18)
    c: Equal(g17,g19)
    c: InternalAlignment(g17,g20)
    c: InternalAlignment(g18,g20)
    c: InternalAlignment(g19,g20)
    c: InternalAlignment(g21,g20)
    c: InternalAlignment(g22,g20)
    c: Block(g20)
    c: Block(g23)
    c: Block(g24)
    c: Block(g25)
    c: Block(g26)
    c: Block(g27)
    c: Block(g28)
    c: Coincident(g29,g28)
    c: Coincident(g29,g0)
    c: Block(g13)
    c: Coincident(g31,g30)
    c: Coincident(g31,g28)
    c: Block(g31)
    c: Coincident(g32,g0)
    c: Vertical(g32)
    c: Coincident(g33,g32)
    c: Horizontal(g33)
    c: Coincident(g34,g33)
    c: Vertical(g34)
    c: Block(g33)
    c: Coincident(g35,g13)
    c: Coincident(g35,g34)
    c: Horizontal(g35)
    c: Coincident(g36,g13)
    c: Coincident(g36,g20)
    c: Coincident(g37,g20)
    c: Coincident(g37,g30)
    c: Block(g30)
    c: Coincident(g38,g1)
    c: Coincident(g38,g2)
    c: Coincident(g39,g1)
    c: Coincident(g39,g2)
    c: Coincident(g40,g3)
    c: Coincident(g40,g4)
    c: Coincident(g41,g3)
    c: Coincident(g41,g4)
    c: Coincident(g42,g5)
    c: Coincident(g42,g6)
    c: Coincident(g43,g5)
    c: Coincident(g43,g6)
    c: Coincident(g44,g7)
    c: Coincident(g44,g8)
    c: Coincident(g45,g7)
    c: Coincident(g45,g8)
    c: Distance(g30) = 256
    c: Distance(g33) = 100
FEATURE [Part::Extrusion] Extrude002
  Base = -> Sketch001
  Dir = (1,0,0)
  DirMode = 2
  FaceMakerClass = Part::FaceMakerBullseye
  LengthFwd = 8
  LengthRev = 0
  Solid = true
  Symmetric = false
FEATURE [Sketcher::SketchObject] Sketch002
  FullyConstrained = true
  sketch-geometry (20):
    g0: LineSegment StartX=-2.77179 StartY=-200.304 StartZ=0 EndX=5.22821 EndY=-200.304 EndZ=0
    g1: LineSegment StartX=5.22821 StartY=-200.304 StartZ=0 EndX=5.22821 EndY=-197.304 EndZ=0
    g2: LineSegment StartX=-2.77179 StartY=-200.304 StartZ=0 EndX=-2.77179 EndY=-197.304 EndZ=0
    g3: LineSegment StartX=5.22821 StartY=-197.304 StartZ=0 EndX=8.22821 EndY=-197.304 EndZ=0
    g4: LineSegment StartX=-2.77179 StartY=-197.304 StartZ=0 EndX=-5.77179 EndY=-197.304 EndZ=0
    g5: LineSegment StartX=19.2282 StartY=-203.304 StartZ=0 EndX=19.2282 EndY=-206.304 EndZ=0
    g6: LineSegment StartX=-16.7718 StartY=-203.304 StartZ=0 EndX=-16.7718 EndY=-206.304 EndZ=0
    g7: LineSegment StartX=-16.7718 StartY=-206.304 StartZ=0 EndX=19.2282 EndY=-206.304 EndZ=0
    g8: Circle CenterX=-16.7718 CenterY=-203.304 CenterZ=0 NormalX=0 NormalY=0 NormalZ=1 AngleXU=0 Radius=1
    g9: Circle CenterX=-5.77179 CenterY=-203.304 CenterZ=0 NormalX=0 NormalY=0 NormalZ=1 AngleXU=0 Radius=1
    g10: Circle CenterX=-5.77179 CenterY=-197.304 CenterZ=0 NormalX=0 NormalY=0 NormalZ=1 AngleXU=0 Radius=1
    g11: BSplineCurve PolesCount=3 KnotsCount=2 Degree=2 IsPeriodic=0
    g12: GeomPoint X=-16.7718 Y=-203.304 Z=0
    g13: GeomPoint X=-5.77179 Y=-197.304 Z=0
    g14: Circle CenterX=19.2282 CenterY=-203.304 CenterZ=0 NormalX=0 NormalY=0 NormalZ=1 AngleXU=0 Radius=1
    g15: Circle CenterX=8.22821 CenterY=-203.304 CenterZ=0 NormalX=0 NormalY=0 NormalZ=1 AngleXU=0 Radius=1
    g16: Circle CenterX=8.22821 CenterY=-197.304 CenterZ=0 NormalX=0 NormalY=0 NormalZ=1 AngleXU=0 Radius=1
    g17: BSplineCurve PolesCount=3 KnotsCount=2 Degree=2 IsPeriodic=0
    g18: GeomPoint X=19.2282 Y=-203.304 Z=0
    g19: GeomPoint X=8.22821 Y=-197.304 Z=0
  constraints (41):
    c: Horizontal(g0)
    c: Distance(g0) = 8
    c: Coincident(g1,g0)
    c: Vertical(g1)
    c: Distance(g1) = 3
    c: Coincident(g2,g0)
    c: Vertical(g2)
    c: Distance(g2) = 3
    c: Coincident(g3,g1)
    c: Horizontal(g3)
    c: Distance(g3) = 3
    c: Coincident(g4,g2)
    c: Horizontal(g4)
    c: Distance(g4) = 3
    c: Vertical(g5)
    c: Vertical(g6)
    c: Coincident(g7,g6)
    c: Coincident(g7,g5)
    c: Weight(g8) = 1
    c: Equal(g8,g9)
    c: Equal(g8,g10)
    c: Coincident(g11,g4)
    c: InternalAlignment(g8,g11)
    c: InternalAlignment(g9,g11)
    c: InternalAlignment(g10,g11)
    c: InternalAlignment(g12,g11)
    c: InternalAlignment(g13,g11)
    c: Coincident(g17,g5)
    c: Weight(g14) = 1
    c: Equal(g14,g15)
    c: Equal(g14,g16)
    c: Coincident(g17,g3)
    c: InternalAlignment(g14,g17)
    c: InternalAlignment(g15,g17)
    c: InternalAlignment(g16,g17)
    c: InternalAlignment(g18,g17)
    c: InternalAlignment(g19,g17)
    c: Block(g7)
    c: Block(g17)
    c: Block(g11)
    c: Block(g6)
FEATURE [Part::Extrusion] Extrude003
  Base = -> Sketch002
  Dir = (0,0,1)
  DirMode = 2
  FaceMakerClass = Part::FaceMakerBullseye
  LengthFwd = 260
  LengthRev = 0
  Solid = true
  Symmetric = false
FEATURE [Part::Extrusion] Extrude
  Base = -> Sketch
  Dir = (0,0,1)
  DirMode = 2
  FaceMakerClass = Part::FaceMakerBullseye
  LengthFwd = 14
  LengthRev = 0
  Solid = true
  Symmetric = false
